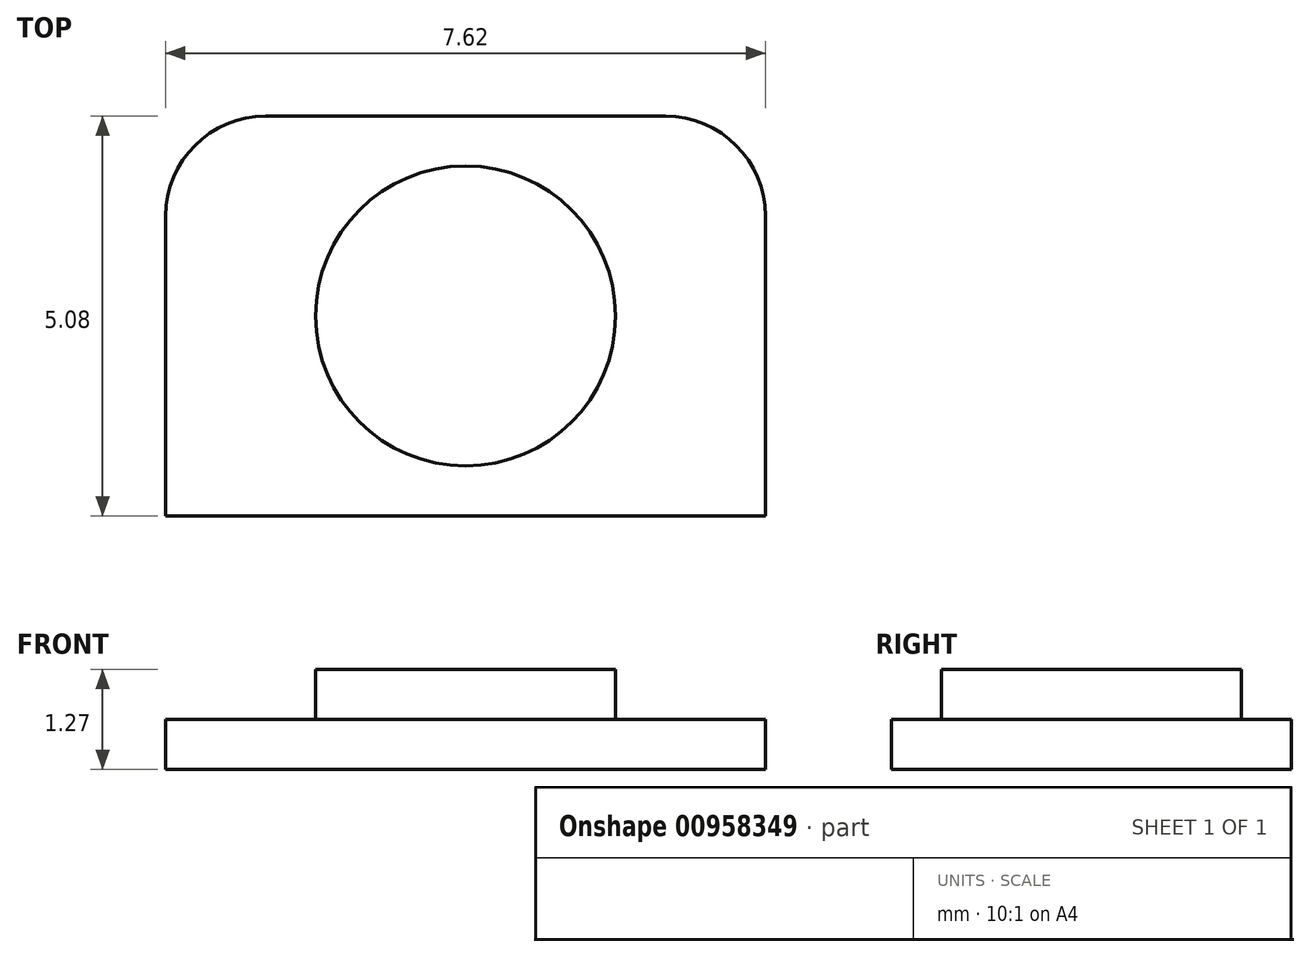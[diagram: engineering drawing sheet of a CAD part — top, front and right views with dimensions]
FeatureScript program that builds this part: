
annotation { "Feature Type Name" : "Feature", "Feature Type Description" : "" }
export const myFeature = defineFeature(function(context is Context, id is Id, definition is map)
    precondition{}
    {
        {
            var Q0;
            Q0=qCreatedBy(makeId("Top.planeOp"),FACE);
            var sketch = newSketch(context, id + "F0", { "sketchPlane" : qUnion([Q0])});
            skLineSegment(sketch, "E0.bottom", {"start": v(3.81, -2.54) * mm, "end": v(-3.81, -2.54) * mm});
            skLineSegment(sketch, "E0.top", {"start": v(2.54, 2.54) * mm, "end": v(-2.54, 2.54) * mm});
            skLineSegment(sketch, "E0.left", {"start": v(3.81, -2.54) * mm, "end": v(3.81, 1.27) * mm});
            skLineSegment(sketch, "E0.right", {"start": v(-3.81, -2.54) * mm, "end": v(-3.81, 1.27) * mm});
            skPoint(sketch, "E0.middle", {"position": v(0, 0) * mm});
            skPoint(sketch, "E1.visualSharp", {"position": v(-3.81, 2.54) * mm});
            skArc(sketch, "E1.filletArc", {"start": v(-2.54, 2.54) * mm, "mid": v(-3.44, 2.17) * mm, "end": v(-3.81, 1.27) * mm});
            skPoint(sketch, "E2.visualSharp", {"position": v(3.81, 2.54) * mm});
            skArc(sketch, "E2.filletArc", {"start": v(3.81, 1.27) * mm, "mid": v(3.44, 2.17) * mm, "end": v(2.54, 2.54) * mm});
            skSolve(sketch);
        }
        {
            var Q0;
            Q0 = qSketchRegion(id + "F0", true);
            extrude(context, id + "F1", {"entities" : qUnion([Q0]), "depth" : 0.64 * mm, "offsetDistance" : 25.4 * mm});
        }
        {
            var Q0;
            Q0=makeQuery(id+"F1.opExtrude","CAP_FACE",FACE,{"disambiguationData":[OSD([sQuery(id+"F0.wireOp",EDGE,"E0.bottom"),sQuery(id+"F0.wireOp",EDGE,"E0.top"),sQuery(id+"F0.wireOp",EDGE,"E0.left"),sQuery(id+"F0.wireOp",EDGE,"E0.right"),sQuery(id+"F0.wireOp",EDGE,"E1.filletArc"),sQuery(id+"F0.wireOp",EDGE,"E2.filletArc")])],"isStart":false});
            var sketch = newSketch(context, id + "F2", { "sketchPlane" : qUnion([Q0])});
            skCircle(sketch, "E3", {"center": v(0, 0) * mm, "radius": 1.9 * mm});
            skSolve(sketch);
        }
        {
            var Q0;
            Q0 = qSketchRegion(id + "F2", true);
            extrude(context, id + "F3", {"entities" : qUnion([Q0]), "operationType" : NewBodyOperationType.ADD, "depth" : 0.64 * mm, "offsetDistance" : 25.4 * mm});
        }
    });
